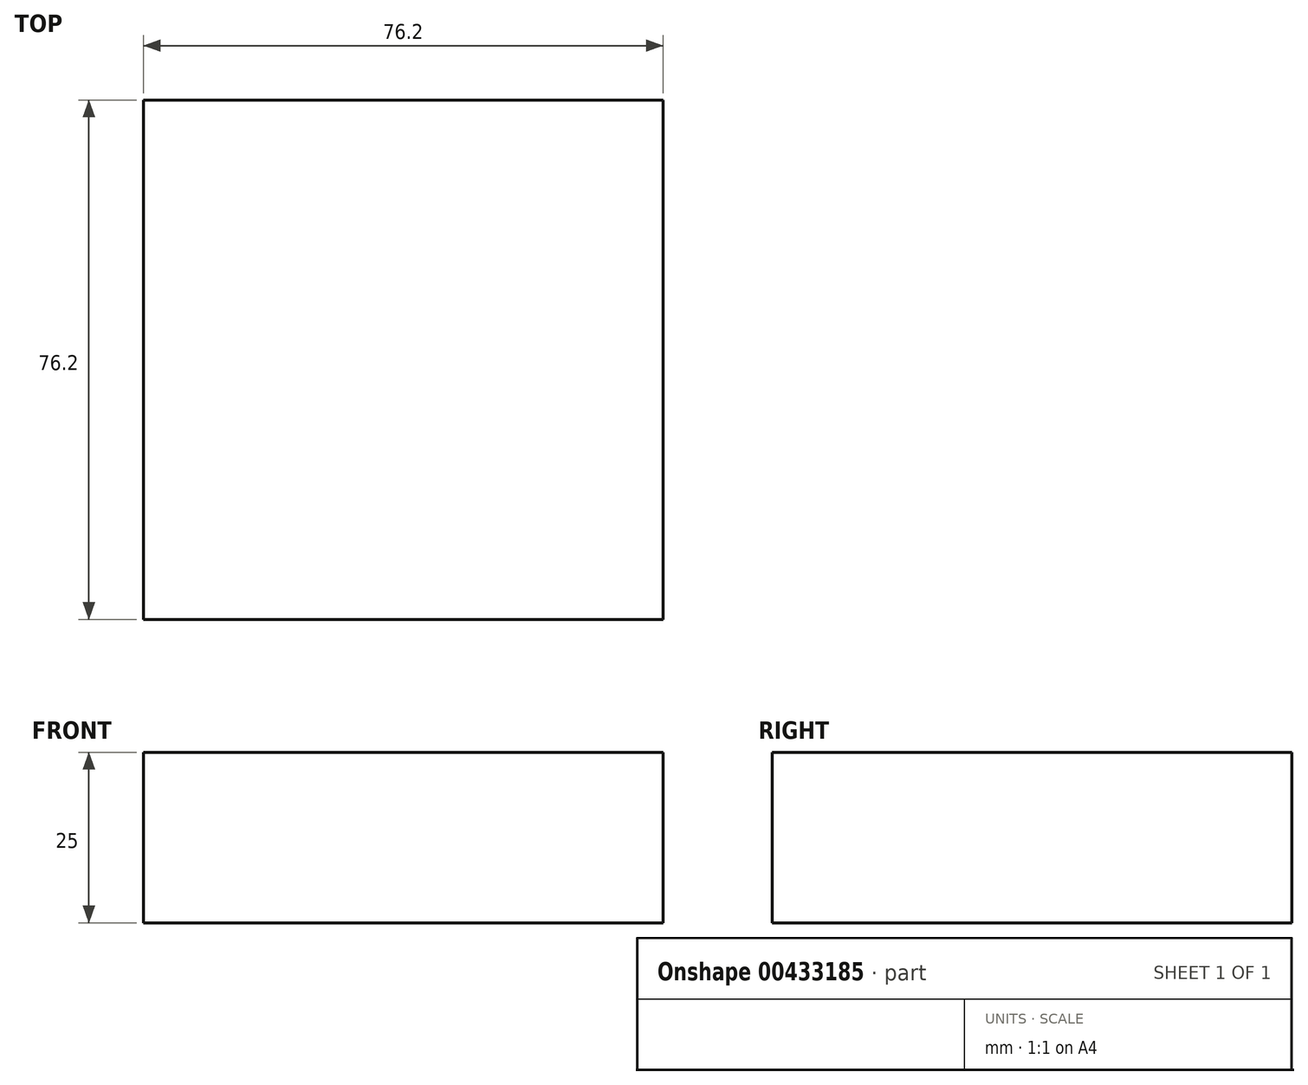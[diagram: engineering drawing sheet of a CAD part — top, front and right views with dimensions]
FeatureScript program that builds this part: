
annotation { "Feature Type Name" : "Feature", "Feature Type Description" : "" }
export const myFeature = defineFeature(function(context is Context, id is Id, definition is map)
    precondition{}
    {
        {
            var Q0;
            Q0=qCreatedBy(makeId("Top.planeOp"),FACE);
            var sketch = newSketch(context, id + "F0", { "sketchPlane" : qUnion([Q0])});
            skLineSegment(sketch, "E0.bottom", {"start": v(-38.47, 34.65) * mm, "end": v(37.73, 34.65) * mm});
            skLineSegment(sketch, "E0.top", {"start": v(-38.47, -41.55) * mm, "end": v(37.73, -41.55) * mm});
            skLineSegment(sketch, "E0.left", {"start": v(-38.47, 34.65) * mm, "end": v(-38.47, -41.55) * mm});
            skLineSegment(sketch, "E0.right", {"start": v(37.73, 34.65) * mm, "end": v(37.73, -41.55) * mm});
            skSolve(sketch);
        }
        {
            var Q0;
            Q0=makeQuery(id+"F0.imprint","IMPRINT",FACE,{"disambiguationData":[TD([[makeQuery(id+"F0.imprint","IMPRINT",EDGE,{"derivedFrom":sQuery(id+"F0.wireOp",EDGE,"E0.bottom")}),-1.0]])]});
            extrude(context, id + "F1", {"entities" : qUnion([Q0]), "depth" : 25 * mm});
        }
    });
